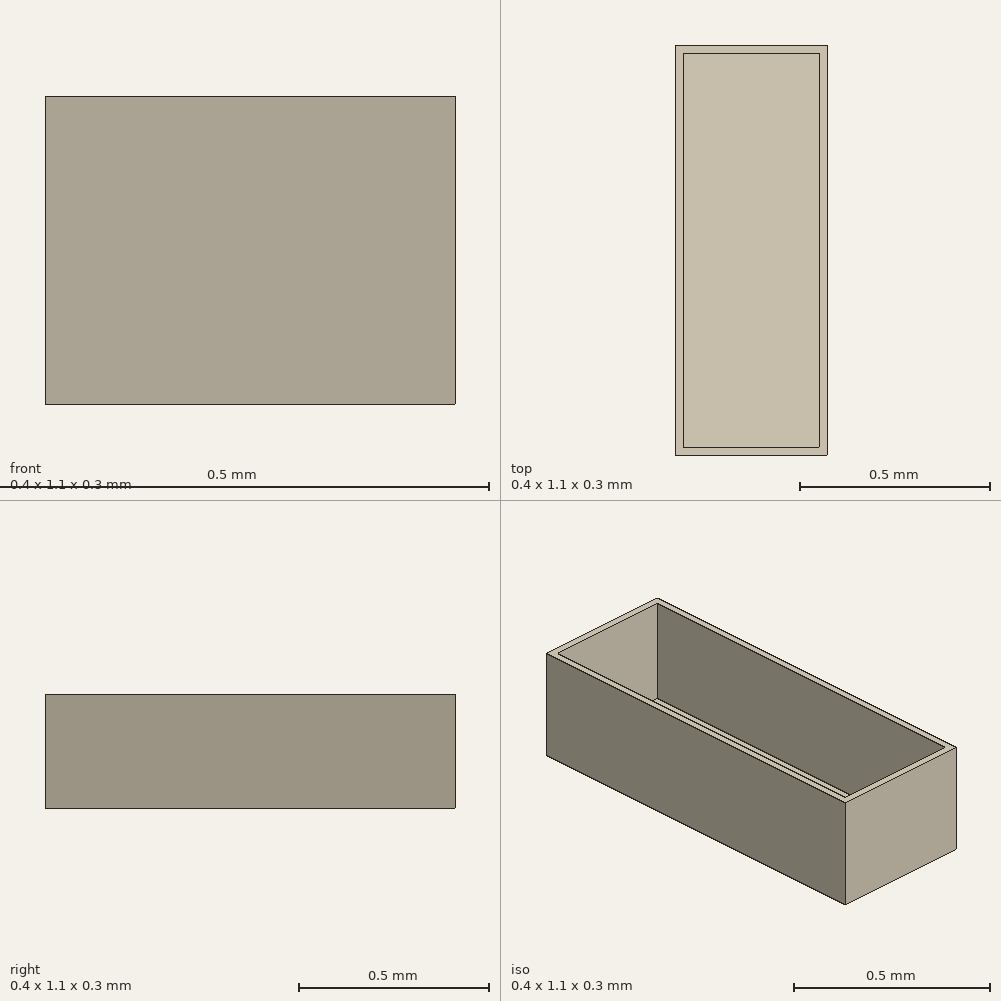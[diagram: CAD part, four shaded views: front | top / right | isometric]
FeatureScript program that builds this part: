
annotation { "Feature Type Name" : "Feature", "Feature Type Description" : "" }
export const myFeature = defineFeature(function(context is Context, id is Id, definition is map)
    precondition{}
    {
        {
            var Q0;
            Q0=qCreatedBy(makeId("Top.planeOp"),FACE);
            var sketch = newSketch(context, id + "F0", { "sketchPlane" : qUnion([Q0])});
            skLineSegment(sketch, "E0.bottom", {"start": v(-0.2, 0.54) * mm, "end": v(0.2, 0.54) * mm});
            skLineSegment(sketch, "E0.top", {"start": v(-0.2, -0.54) * mm, "end": v(0.2, -0.54) * mm});
            skLineSegment(sketch, "E0.left", {"start": v(-0.2, 0.54) * mm, "end": v(-0.2, -0.54) * mm});
            skLineSegment(sketch, "E0.right", {"start": v(0.2, 0.54) * mm, "end": v(0.2, -0.54) * mm});
            skPoint(sketch, "E0.middle", {"position": v(0, 0) * mm});
            skSolve(sketch);
        }
        {
            var Q0;
            Q0 = qSketchRegion(id + "F0", true);
            extrude(context, id + "F1", {"entities" : qUnion([Q0]), "oppositeDirection" : true, "depth" : 0.3 * mm, "offsetDistance" : 25 * mm});
        }
        {
            var Q0;
            Q0=makeQuery(id+"F1.opExtrude","CAP_FACE",FACE,{"disambiguationData":[OSD([sQuery(id+"F0.wireOp",EDGE,"E0.bottom"),sQuery(id+"F0.wireOp",EDGE,"E0.top"),sQuery(id+"F0.wireOp",EDGE,"E0.left"),sQuery(id+"F0.wireOp",EDGE,"E0.right")])],"isStart":true});
            shell(context, id + "F2", {"entities" : qUnion([Q0]), "thickness" : 0.02 * mm});
        }
    });
